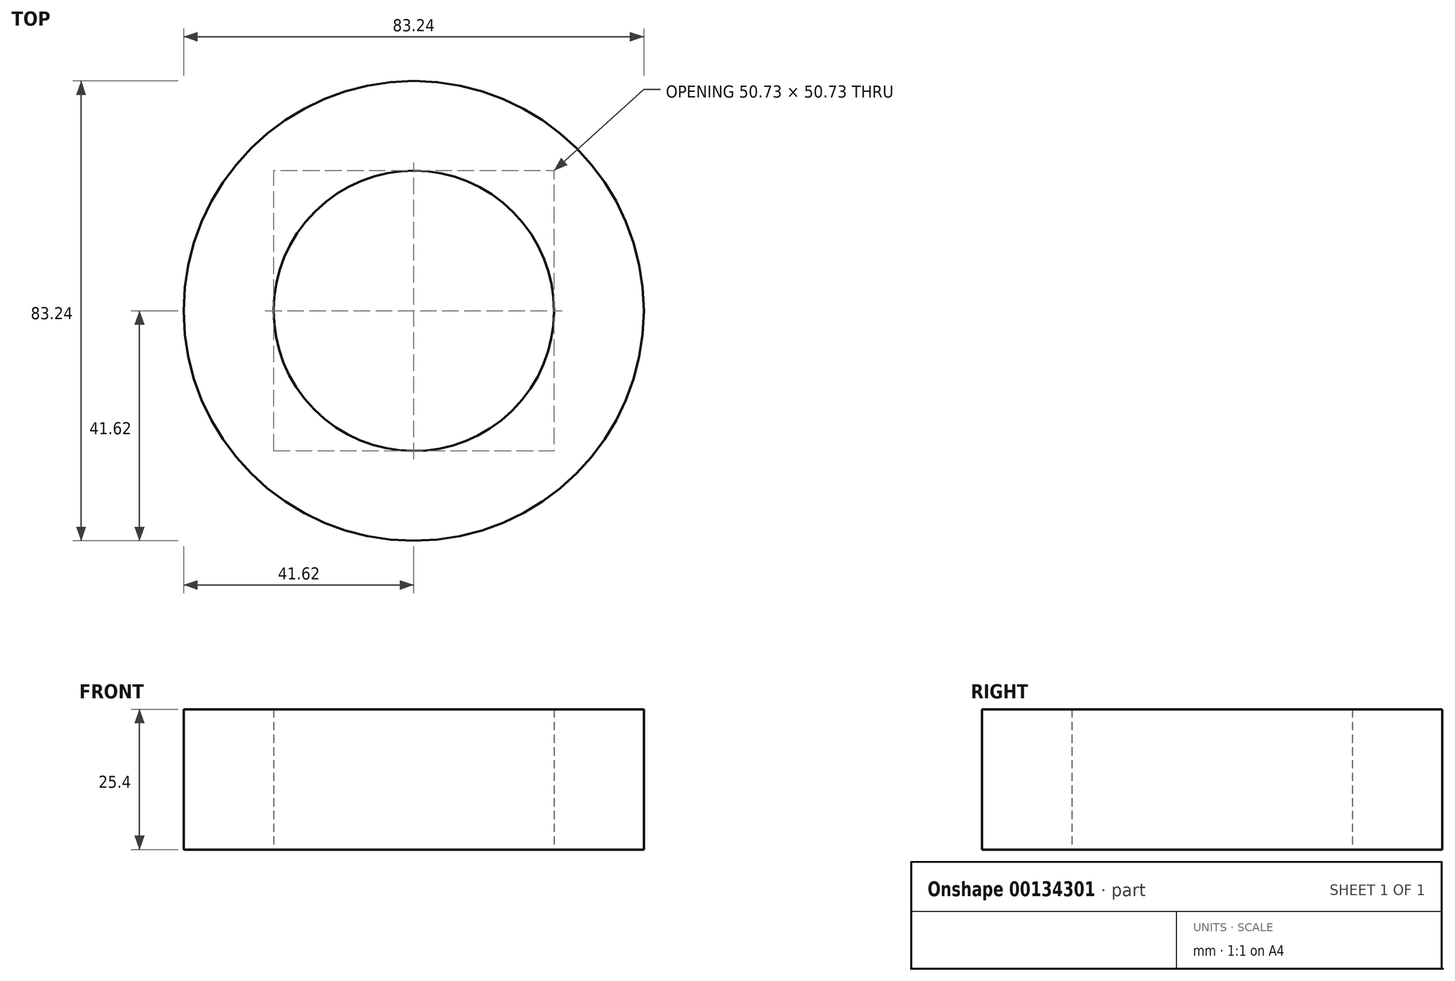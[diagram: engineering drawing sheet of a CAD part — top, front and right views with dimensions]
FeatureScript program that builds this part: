
annotation { "Feature Type Name" : "Feature", "Feature Type Description" : "" }
export const myFeature = defineFeature(function(context is Context, id is Id, definition is map)
    precondition{}
    {
        {
            var Q0;
            Q0=qCreatedBy(makeId("Top.planeOp"),FACE);
            var sketch = newSketch(context, id + "F0", { "sketchPlane" : qUnion([Q0])});
            skLineSegment(sketch, "E0.bottom", {"start": v(29.58, 29.28) * mm, "end": v(-29.58, 29.28) * mm});
            skLineSegment(sketch, "E0.top", {"start": v(29.58, -29.28) * mm, "end": v(-29.58, -29.28) * mm});
            skLineSegment(sketch, "E0.left", {"start": v(29.58, 29.28) * mm, "end": v(29.58, -29.28) * mm});
            skLineSegment(sketch, "E0.right", {"start": v(-29.58, 29.28) * mm, "end": v(-29.58, -29.28) * mm});
            skPoint(sketch, "E0.middle", {"position": v(0, 0) * mm});
            skCircle(sketch, "E1", {"center": v(0, 0) * mm, "radius": 41.62 * mm});
            skCircle(sketch, "E2", {"center": v(0, 0) * mm, "radius": 25.37 * mm});
            skLineSegment(sketch, "E3.bottom", {"start": v(-17.88, 17.99) * mm, "end": v(-14.83, 17.99) * mm});
            skLineSegment(sketch, "E3.top", {"start": v(-17.88, -17.99) * mm, "end": v(-1.43, -17.99) * mm});
            skLineSegment(sketch, "E3.left", {"start": v(-17.88, 17.99) * mm, "end": v(-17.88, 14.93) * mm});
            skLineSegment(sketch, "E3.right", {"start": v(17.88, 17.99) * mm, "end": v(17.88, 1.34) * mm});
            skLineSegment(sketch, "E4.left", {"start": v(-8.23, -3.34) * mm, "end": v(-8.23, -3.38) * mm});
            skArc(sketch, "E5", {"start": v(2.1, 13.82) * mm, "mid": v(-18.26, 14.35) * mm, "end": v(-8.23, -3.38) * mm});
            skArc(sketch, "E6", {"start": v(14.94, 3.57) * mm, "mid": v(13.36, 14.75) * mm, "end": v(2.1, 13.82) * mm});
            skArc(sketch, "E7", {"start": v(-8.23, -3.34) * mm, "mid": v(-12.89, -10.1) * mm, "end": v(-4.92, -12.05) * mm});
            skArc(sketch, "E8.trimOffspring", {"start": v(-4.92, -12.05) * mm, "mid": v(16.67, -19.06) * mm, "end": v(14.94, 3.57) * mm});
            skPoint(sketch, "E9.orphan", {"position": v(17.88, -17.99) * mm});
            skLineSegment(sketch, "E10.trimOffspring", {"start": v(-17.88, 1.71) * mm, "end": v(-17.88, -17.99) * mm});
            skLineSegment(sketch, "E11.trimOffspring", {"start": v(-1.62, 17.99) * mm, "end": v(17.88, 17.99) * mm});
            skSolve(sketch);
        }
        {
            var Q0;
            Q0 = qSketchRegion(id + "F0", true);
            extrude(context, id + "F1", {"entities" : qUnion([Q0]), "depth" : 25.4 * mm});
        }
    });
